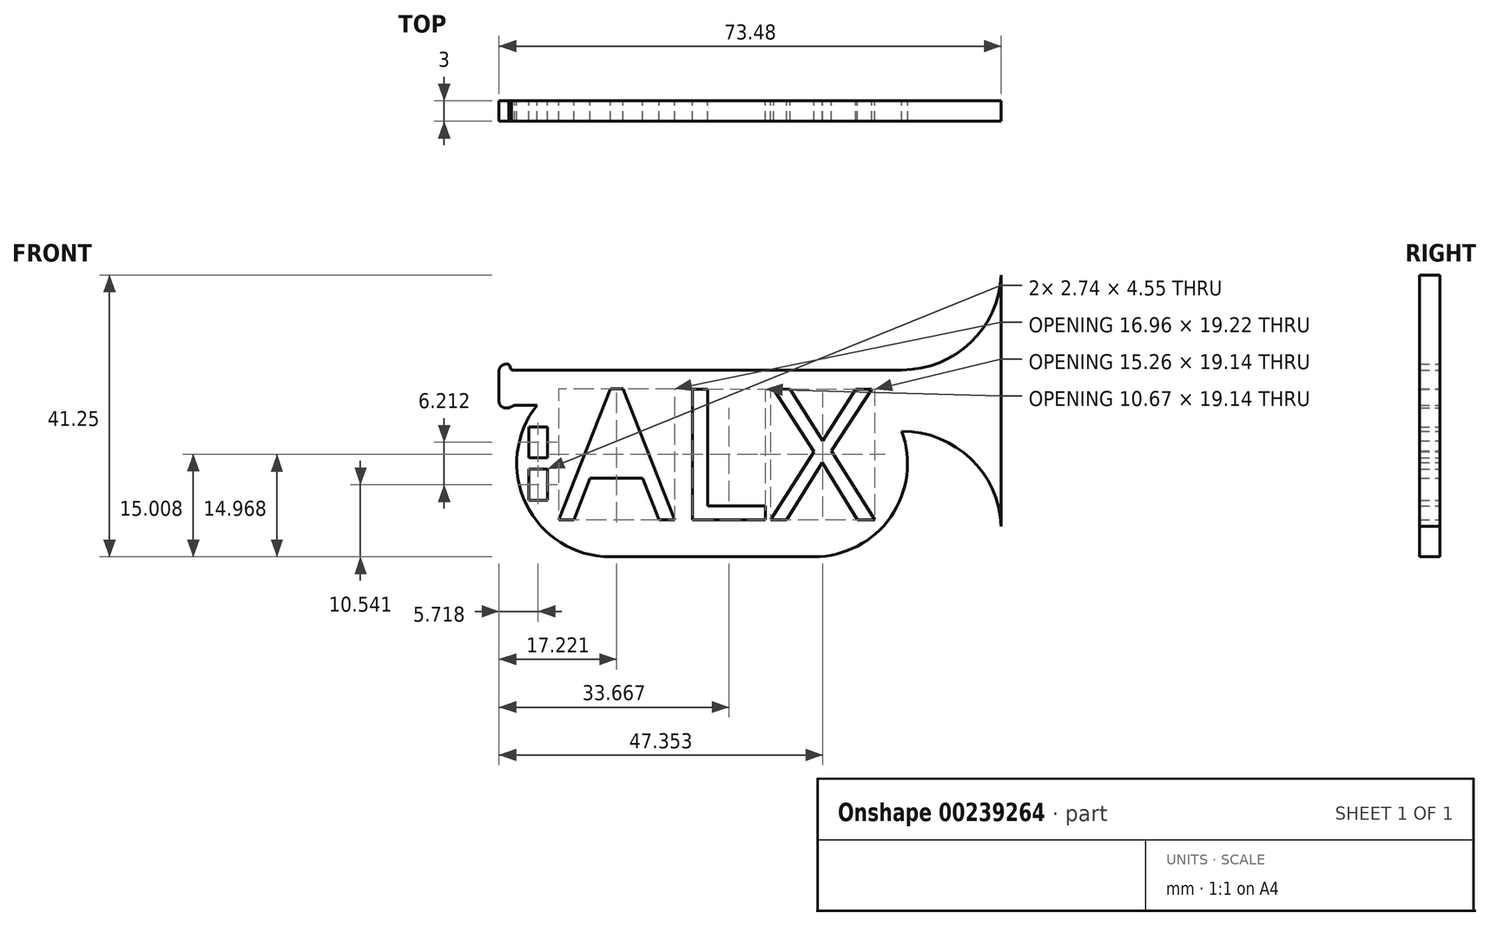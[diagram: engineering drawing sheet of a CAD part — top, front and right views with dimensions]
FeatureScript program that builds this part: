
annotation { "Feature Type Name" : "Feature", "Feature Type Description" : "" }
export const myFeature = defineFeature(function(context is Context, id is Id, definition is map)
    precondition{}
    {
        {
            var Q0;
            Q0=qCreatedBy(makeId("Front.planeOp"),FACE);
            var sketch = newSketch(context, id + "F0", { "sketchPlane" : qUnion([Q0])});
            skArc(sketch, "E0", {"start": v(-10.7, 8.5) * mm, "mid": v(-12.3, -5.95) * mm, "end": v(0, -13.67) * mm});
            skArc(sketch, "E1", {"start": v(29.83, -13.67) * mm, "mid": v(41.04, -7.82) * mm, "end": v(42.66, 4.72) * mm});
            skLineSegment(sketch, "E2", {"start": v(0, 13.67) * mm, "end": v(29.83, 13.67) * mm});
            skLineSegment(sketch, "E3", {"start": v(0, -13.67) * mm, "end": v(29.83, -13.67) * mm});
            skLineSegment(sketch, "E4", {"start": v(0, 13.67) * mm, "end": v(-14.43, 13.67) * mm});
            skLineSegment(sketch, "E5", {"start": v(-14.43, 13.67) * mm, "end": v(-14.83, 14.51) * mm});
            skLineSegment(sketch, "E6", {"start": v(-14.83, 14.51) * mm, "end": v(-15.27, 14.51) * mm});
            skLineSegment(sketch, "E7", {"start": v(-16.27, 13.51) * mm, "end": v(-16.27, 9.1) * mm});
            skLineSegment(sketch, "E8", {"start": v(-15.27, 8.1) * mm, "end": v(-14.83, 8.1) * mm});
            skLineSegment(sketch, "E9", {"start": v(-14.83, 8.1) * mm, "end": v(-13.99, 8.5) * mm});
            skLineSegment(sketch, "E10", {"start": v(-13.99, 8.5) * mm, "end": v(-10.7, 8.5) * mm});
            skPoint(sketch, "E11.visualSharp", {"position": v(-16.27, 14.51) * mm});
            skArc(sketch, "E11.filletArc", {"start": v(-15.27, 14.51) * mm, "mid": v(-15.98, 14.22) * mm, "end": v(-16.27, 13.51) * mm});
            skPoint(sketch, "E12.visualSharp", {"position": v(-16.27, 8.1) * mm});
            skArc(sketch, "E12.filletArc", {"start": v(-16.27, 9.1) * mm, "mid": v(-15.98, 8.4) * mm, "end": v(-15.27, 8.1) * mm});
            skLineSegment(sketch, "E13", {"start": v(29.83, 13.67) * mm, "end": v(42.66, 13.67) * mm});
            skLineSegment(sketch, "E14", {"start": v(42.66, 4.72) * mm, "end": v(42.66, 4.72) * mm});
            skLineSegment(sketch, "E15", {"start": v(42.66, 13.67) * mm, "end": v(42.66, 4.72) * mm, "construction": true});
            skArc(sketch, "E16", {"start": v(42.66, 13.67) * mm, "mid": v(53.19, 18.17) * mm, "end": v(57.21, 28.88) * mm});
            skArc(sketch, "E17", {"start": v(57.21, -9.2) * mm, "mid": v(52.73, 0.68) * mm, "end": v(42.66, 4.72) * mm});
            skLineSegment(sketch, "E18", {"start": v(42.66, 28.23) * mm, "end": v(42.66, -9.84) * mm, "construction": true});
            skLineSegment(sketch, "E19", {"start": v(57.21, 28.88) * mm, "end": v(57.21, -9.2) * mm});
            skLineSegment(sketch, "E20.bottom", {"start": v(-11.92, 5.36) * mm, "end": v(-9.18, 5.36) * mm});
            skLineSegment(sketch, "E20.top", {"start": v(-11.92, -5.4) * mm, "end": v(-9.18, -5.4) * mm});
            skLineSegment(sketch, "E20.left", {"start": v(-11.92, 5.36) * mm, "end": v(-11.92, 0.8) * mm});
            skLineSegment(sketch, "E20.right", {"start": v(-9.18, 5.36) * mm, "end": v(-9.18, 0.8) * mm});
            skPoint(sketch, "E21.endSnap0", {"position": v(-9.18, -0.02) * mm});
            skLineSegment(sketch, "E22.trimOffspring", {"start": v(-11.92, -0.86) * mm, "end": v(-11.92, -5.4) * mm});
            skLineSegment(sketch, "E23.trimOffspring", {"start": v(-9.18, -0.86) * mm, "end": v(-9.18, -5.4) * mm});
            skLineSegment(sketch, "E24", {"start": v(-11.92, 0.8) * mm, "end": v(-9.18, 0.8) * mm});
            skLineSegment(sketch, "E25", {"start": v(-11.92, -0.86) * mm, "end": v(-9.18, -0.86) * mm});
            skPoint(sketch, "E26.orphan", {"position": v(-9.18, 0) * mm});
            skPoint(sketch, "E27.orphan", {"position": v(-11.92, -0.02) * mm});
            skText(sketch, "E28", { "text": "ALX", "fontName": "OpenSans-Regular.ttf"});
            const initialGuessF0  = {"E28": [-0.00753, -0.00827, 1, 0, 0.0193]};
            skSetInitialGuess(sketch, initialGuessF0);
            skSolve(sketch);
        }
        {
            var Q0;
            Q0=makeQuery(id+"F0.imprint","IMPRINT",FACE,{"disambiguationData":[TD([[makeQuery(id+"F0.imprint","IMPRINT",EDGE,{"derivedFrom":sQuery(id+"F0.wireOp",EDGE,"E0")}),1.0]])]});
            extrude(context, id + "F1", {"entities" : qUnion([Q0]), "depth" : 3 * mm});
        }
    });
